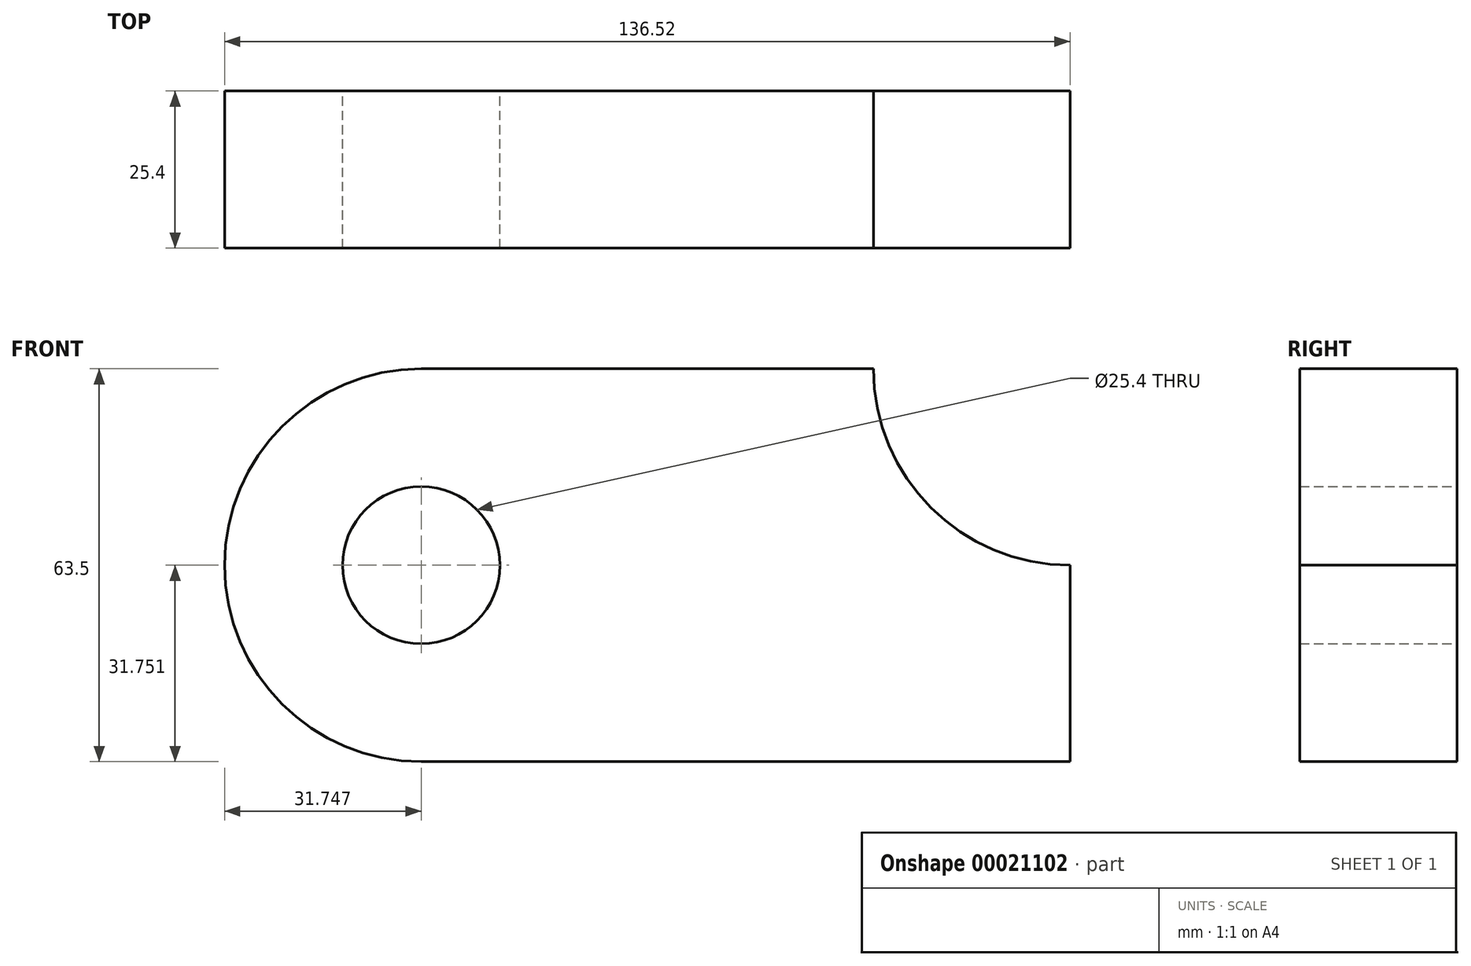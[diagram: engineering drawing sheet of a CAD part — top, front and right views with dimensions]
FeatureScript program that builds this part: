
annotation { "Feature Type Name" : "Feature", "Feature Type Description" : "" }
export const myFeature = defineFeature(function(context is Context, id is Id, definition is map)
    precondition{}
    {
        {
            var Q0;
            Q0=qCreatedBy(makeId("Front.planeOp"),FACE);
            var sketch = newSketch(context, id + "F0", { "sketchPlane" : qUnion([Q0])});
            skLineSegment(sketch, "E0.bottom", {"start": v(-40.44, 37.6) * mm, "end": v(64.33, 37.6) * mm});
            skLineSegment(sketch, "E0.top", {"start": v(-40.44, -25.9) * mm, "end": v(64.33, -25.9) * mm});
            skLineSegment(sketch, "E0.left", {"start": v(-40.44, 37.6) * mm, "end": v(-40.44, -25.9) * mm});
            skLineSegment(sketch, "E0.right", {"start": v(64.33, 37.6) * mm, "end": v(64.33, -25.9) * mm});
            skCircle(sketch, "E1", {"center": v(-40.44, 5.85) * mm, "radius": 31.75 * mm});
            skCircle(sketch, "E2", {"center": v(-40.44, 5.85) * mm, "radius": 12.7 * mm});
            skCircle(sketch, "E3", {"center": v(64.33, 37.6) * mm, "radius": 31.75 * mm});
            skSolve(sketch);
        }
        {
            var Q0;
            {var subQ6=sQuery(id+"F0.wireOp",EDGE,"E0.top");Q0=makeQuery(id+"F0.imprint","IMPRINT",FACE,{"disambiguationData":[TD([[makeQuery(id+"F0.imprint","IMPRINT",EDGE,{"derivedFrom":subQ6}),1.0]])]});}
            var Q1;
            {var subQ0=sQuery(id+"F0.wireOp",EDGE,"E2");var subQ1=sQuery(id+"F0.wireOp",EDGE,"E0.left");var subQ3=makeQuery(id+"F0.imprint","INTERSECT",VERTEX,{"disambiguationData":[OD(0.0)],"derivedFrom":[subQ1,subQ0]});Q1=makeQuery(id+"F0.imprint","IMPRINT",FACE,{"disambiguationData":[TD([[makeQuery(id+"F0.imprint","IMPRINT",EDGE,{"disambiguationData":[TD([[subQ3,-1.0]])],"derivedFrom":subQ0}),-1.0]])]});}
            var Q2;
            {var subQ0=sQuery(id+"F0.wireOp",EDGE,"E2");var subQ1=sQuery(id+"F0.wireOp",EDGE,"E0.left");var subQ3=makeQuery(id+"F0.imprint","INTERSECT",VERTEX,{"disambiguationData":[OD(0.0)],"derivedFrom":[subQ1,subQ0]});Q2=makeQuery(id+"F0.imprint","IMPRINT",FACE,{"disambiguationData":[TD([[makeQuery(id+"F0.imprint","IMPRINT",EDGE,{"disambiguationData":[TD([[subQ3,1.0]])],"derivedFrom":subQ0}),-1.0]])]});}
            extrude(context, id + "F1", {"entities" : qUnion([Q0, Q1, Q2]), "depth" : 25.4 * mm});
        }
    });
